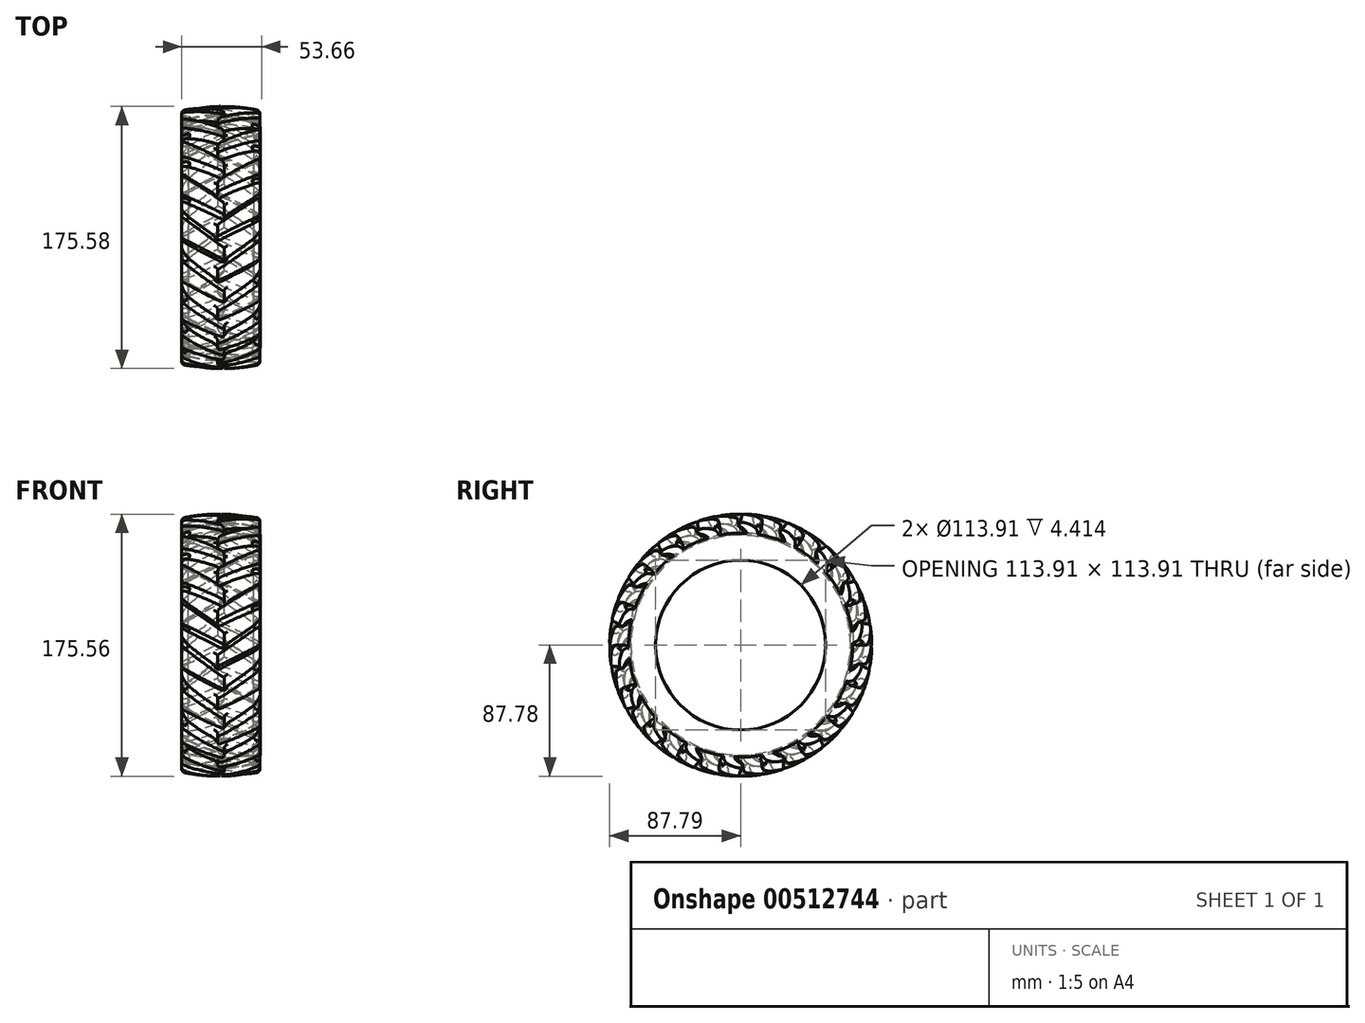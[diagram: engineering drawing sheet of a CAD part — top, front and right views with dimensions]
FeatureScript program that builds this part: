
annotation { "Feature Type Name" : "Feature", "Feature Type Description" : "" }
export const myFeature = defineFeature(function(context is Context, id is Id, definition is map)
    precondition{}
    {
        {
            var Q0;
            Q0=qCreatedBy(makeId("Top.planeOp"),FACE);
            var sketch = newSketch(context, id + "F0", { "sketchPlane" : qUnion([Q0])});
            skLineSegment(sketch, "E0", {"start": v(-41.36, 0) * mm, "end": v(39.08, 0) * mm});
            skLineSegment(sketch, "E1", {"start": v(0, 0) * mm, "end": v(0, 69.17) * mm});
            skLineSegment(sketch, "E2.bottom", {"start": v(26.28, 56.34) * mm, "end": v(-26.28, 56.34) * mm});
            skLineSegment(sketch, "E2.left", {"start": v(26.28, 56.34) * mm, "end": v(26.28, 73.43) * mm});
            skLineSegment(sketch, "E2.right", {"start": v(-26.28, 56.34) * mm, "end": v(-26.28, 73.43) * mm});
            skPoint(sketch, "E2.middle", {"position": v(0, 69.17) * mm});
            skArc(sketch, "E3", {"start": v(-21.6, 79.56) * mm, "mid": v(0, 82.44) * mm, "end": v(21.6, 79.56) * mm});
            skPoint(sketch, "E4.orphan", {"position": v(-26.28, 82) * mm});
            skPoint(sketch, "E5.orphan", {"position": v(26.28, 82) * mm});
            skPoint(sketch, "E6.visualSharp", {"position": v(-26.28, 78.14) * mm});
            skArc(sketch, "E6.filletArc", {"start": v(-21.6, 79.56) * mm, "mid": v(-24.97, 77.3) * mm, "end": v(-26.28, 73.43) * mm});
            skPoint(sketch, "E7.visualSharp", {"position": v(26.28, 78.14) * mm});
            skArc(sketch, "E7.filletArc", {"start": v(26.28, 73.43) * mm, "mid": v(24.97, 77.3) * mm, "end": v(21.6, 79.56) * mm});
            skSolve(sketch);
        }
        {
            var Q0;
            Q0=qSketchRegion(id+"F0",true);
            var Q1;
            Q1=sQuery(id+"F0.wireOp",EDGE,"E0");
            revolve(context, id + "F1", {"entities" : qUnion([Q0]), "axis" : qUnion([Q1]), "revolveType" : RevolveType.FULL});
        }
        {
            var Q0;
            Q0=qCreatedBy(makeId("Top.planeOp"),FACE);
            var sketch = newSketch(context, id + "F2", { "sketchPlane" : qUnion([Q0])});
            skLineSegment(sketch, "E8", {"start": v(-26.25, 13.83) * mm, "end": v(2.16, -6.94) * mm});
            skLineSegment(sketch, "E9", {"start": v(2.16, -6.94) * mm, "end": v(2.16, -14.96) * mm});
            skLineSegment(sketch, "E10", {"start": v(2.16, -14.96) * mm, "end": v(-26.25, -0.3) * mm});
            skLineSegment(sketch, "E11", {"start": v(-26.25, 13.83) * mm, "end": v(-26.25, 0) * mm});
            skLineSegment(sketch, "E12", {"start": v(-26.25, 0) * mm, "end": v(-26.25, -0.3) * mm});
            skPoint(sketch, "E13.orphan", {"position": v(-26.83, 0) * mm});
            skLineSegment(sketch, "E14", {"start": v(-49.96, 0) * mm, "end": v(51.5, 0) * mm});
            skSolve(sketch);
        }
        {
            var Q0;
            Q0=makeQuery(id+"F2.imprint","IMPRINT",FACE,{"disambiguationData":[TD([[makeQuery(id+"F2.imprint","IMPRINT",EDGE,{"derivedFrom":sQuery(id+"F2.wireOp",EDGE,"E8")}),-1.0]])]});
            var Q1;
            {var subQ1=sQuery(id+"F2.wireOp",EDGE,"E9");Q1=makeQuery(id+"F2.imprint","IMPRINT",FACE,{"disambiguationData":[TD([[makeQuery(id+"F2.imprint","IMPRINT",EDGE,{"derivedFrom":subQ1}),-1.0]])]});}
            extrude(context, id + "F3", {"entities" : qUnion([Q0, Q1]), "operationType" : NewBodyOperationType.ADD, "depth" : 88.9 * mm});
        }
        {
            var Q0;
            Q0=qCreatedBy(makeId("Top.planeOp"),FACE);
            var Q1;
            Q1=sQuery(id+"F2.wireOp",EDGE,"E14");
            cPlane(context, id + "F4", {"entities" : qUnion([Q0, Q1]), "cplaneType" : CPlaneType.LINE_ANGLE, "offset" : 152.4 * mm, "angle" : 10 * degree, "width" : 152.4 * mm, "height" : 152.4 * mm});
        }
        {
            var Q0;
            Q0=qCreatedBy(id+"F4.planeOp",FACE);
            var sketch = newSketch(context, id + "F5", { "sketchPlane" : qUnion([Q0])});
            skLineSegment(sketch, "E15", {"start": v(-2.2, 14.33) * mm, "end": v(-2.2, 6.63) * mm});
            skLineSegment(sketch, "E16", {"start": v(-2.2, 6.63) * mm, "end": v(26.07, -12.68) * mm});
            skLineSegment(sketch, "E17", {"start": v(26.07, -12.68) * mm, "end": v(26.07, 0) * mm});
            skLineSegment(sketch, "E18", {"start": v(26.07, 0) * mm, "end": v(-2.2, 14.33) * mm});
            skSolve(sketch);
        }
        {
            var Q0;
            Q0=makeQuery(id+"F5.imprint","IMPRINT",FACE,{"disambiguationData":[TD([[makeQuery(id+"F5.imprint","IMPRINT",EDGE,{"derivedFrom":sQuery(id+"F5.wireOp",EDGE,"E15")}),1.0]])]});
            extrude(context, id + "F6", {"entities" : qUnion([Q0]), "operationType" : NewBodyOperationType.ADD, "oppositeDirection" : true, "depth" : 88.9 * mm});
        }
        {
            var Q0;
            Q0=qCreatedBy(makeId("Front.planeOp"),FACE);
            var sketch = newSketch(context, id + "F7", { "sketchPlane" : qUnion([Q0])});
            skArc(sketch, "E19", {"start": v(33.67, -83.2) * mm, "mid": v(-0.3, -87.8) * mm, "end": v(-34.27, -83.04) * mm});
            skLineSegment(sketch, "E20", {"start": v(-34.27, -83.04) * mm, "end": v(-34.27, -99.42) * mm});
            skLineSegment(sketch, "E21", {"start": v(-34.27, -99.42) * mm, "end": v(37.55, -99.42) * mm});
            skLineSegment(sketch, "E22", {"start": v(37.55, -99.42) * mm, "end": v(33.67, -83.2) * mm});
            skArc(sketch, "E23", {"start": v(21.86, -73.58) * mm, "mid": v(0, -75.71) * mm, "end": v(-21.86, -73.58) * mm});
            skLineSegment(sketch, "E24", {"start": v(-21.86, -73.58) * mm, "end": v(-21.86, -56.95) * mm});
            skLineSegment(sketch, "E25", {"start": v(-21.86, 0) * mm, "end": v(21.86, 0) * mm});
            skLineSegment(sketch, "E26", {"start": v(21.86, -56.95) * mm, "end": v(21.86, -73.58) * mm});
            skLineSegment(sketch, "E27", {"start": v(21.86, -56.95) * mm, "end": v(33.74, -56.95) * mm});
            skLineSegment(sketch, "E28", {"start": v(33.74, -56.95) * mm, "end": v(33.74, 0) * mm});
            skLineSegment(sketch, "E29", {"start": v(33.74, 0) * mm, "end": v(21.86, 0) * mm});
            skLineSegment(sketch, "E30", {"start": v(0, 0) * mm, "end": v(0, -57.21) * mm});
            skPoint(sketch, "E30.endSnap0", {"position": v(0, 0) * mm});
            skLineSegment(sketch, "E31.MirrorCS", {"start": v(-21.86, -56.95) * mm, "end": v(-33.74, -56.95) * mm});
            skLineSegment(sketch, "E32.MirrorCS", {"start": v(-33.74, -56.95) * mm, "end": v(-33.74, 0) * mm});
            skLineSegment(sketch, "E33.MirrorCS", {"start": v(-33.74, 0) * mm, "end": v(-21.86, 0) * mm});
            skSolve(sketch);
        }
        {
            var Q0;
            Q0=qSketchRegion(id+"F7",true);
            var Q1;
            Q1=sQuery(id+"F2.wireOp",EDGE,"E14");
            revolve(context, id + "F8", {"operationType" : NewBodyOperationType.REMOVE, "entities" : qUnion([Q0]), "axis" : qUnion([Q1]), "revolveType" : RevolveType.FULL, "oppositeDirection" : true});
        }
        {
            var Q0;
            Q0=makeQuery(id+"F6.boolean.opBoolean","INTERSECT",EDGE,{"derivedFrom":[makeQuery(id+"F1.opRevolve","SWEPT_FACE",FACE,{"disambiguationData":[OSD([sQuery(id+"F0.wireOp",EDGE,"E3")])]}),makeQuery(id+"F6.opExtrude","SWEPT_FACE",FACE,{"disambiguationData":[OSD([sQuery(id+"F5.wireOp",EDGE,"E18")])]})]});
            var Q1;
            Q1=makeQuery(id+"F6.boolean.opBoolean","INTERSECT",EDGE,{"derivedFrom":[makeQuery(id+"F1.opRevolve","SWEPT_FACE",FACE,{"disambiguationData":[OSD([sQuery(id+"F0.wireOp",EDGE,"E3")])]}),makeQuery(id+"F6.opExtrude","SWEPT_FACE",FACE,{"disambiguationData":[OSD([sQuery(id+"F5.wireOp",EDGE,"E16")])]})]});
            var Q2;
            Q2=makeQuery(id+"F3.boolean.opBoolean","INTERSECT",EDGE,{"derivedFrom":[makeQuery(id+"F1.opRevolve","SWEPT_FACE",FACE,{"disambiguationData":[OSD([sQuery(id+"F0.wireOp",EDGE,"E3")])]}),makeQuery(id+"F3.opExtrude","SWEPT_FACE",FACE,{"disambiguationData":[OSD([sQuery(id+"F2.wireOp",EDGE,"E8")])]})]});
            var Q3;
            Q3=makeQuery(id+"F3.boolean.opBoolean","INTERSECT",EDGE,{"derivedFrom":[makeQuery(id+"F1.opRevolve","SWEPT_FACE",FACE,{"disambiguationData":[OSD([sQuery(id+"F0.wireOp",EDGE,"E3")])]}),makeQuery(id+"F3.opExtrude","SWEPT_FACE",FACE,{"disambiguationData":[OSD([sQuery(id+"F2.wireOp",EDGE,"E10")])]})]});
            var Q4;
            Q4=makeQuery(id+"F6.boolean.opBoolean","INTERSECT",EDGE,{"derivedFrom":[makeQuery(id+"F1.opRevolve","SWEPT_FACE",FACE,{"disambiguationData":[OSD([sQuery(id+"F0.wireOp",EDGE,"E3")])]}),makeQuery(id+"F6.opExtrude","SWEPT_FACE",FACE,{"disambiguationData":[OSD([sQuery(id+"F5.wireOp",EDGE,"E15")])]})]});
            var Q5;
            Q5=makeQuery(id+"F3.boolean.opBoolean","INTERSECT",EDGE,{"derivedFrom":[makeQuery(id+"F1.opRevolve","SWEPT_FACE",FACE,{"disambiguationData":[OSD([sQuery(id+"F0.wireOp",EDGE,"E3")])]}),makeQuery(id+"F3.opExtrude","SWEPT_FACE",FACE,{"disambiguationData":[OSD([sQuery(id+"F2.wireOp",EDGE,"E9")])]})]});
            var Q6;
            {var subQ2=sQuery(id+"F2.wireOp",EDGE,"E12");var subQ3=sQuery(id+"F2.wireOp",EDGE,"E11");Q6=makeQuery(id+"F8.boolean.opBoolean","INTERSECT",EDGE,{"derivedFrom":[makeQuery(id+"F3.boolean.opBoolean","SPLIT",FACE,{"disambiguationData":[TD([makeQuery(id+"F1.opRevolve","SWEPT_FACE",FACE,{"disambiguationData":[OSD([sQuery(id+"F0.wireOp",EDGE,"E6.filletArc")])]})])],"derivedFrom":makeQuery(id+"F3.opExtrude","SWEPT_FACE",FACE,{"disambiguationData":[OSD([subQ3,subQ2])]})}),makeQuery(id+"F8.opRevolve","SWEPT_FACE",FACE,{"disambiguationData":[OSD([sQuery(id+"F7.wireOp",EDGE,"E19")])]})]});}
            var Q7;
            {var subQ2=sQuery(id+"F2.wireOp",EDGE,"E9");Q7=makeQuery(id+"F8.boolean.opBoolean","INTERSECT",EDGE,{"derivedFrom":[makeQuery(id+"F3.boolean.opBoolean","SPLIT",FACE,{"disambiguationData":[TD([makeQuery(id+"F1.opRevolve","SWEPT_FACE",FACE,{"disambiguationData":[OSD([sQuery(id+"F0.wireOp",EDGE,"E3")])]})])],"derivedFrom":makeQuery(id+"F3.opExtrude","SWEPT_FACE",FACE,{"disambiguationData":[OSD([subQ2])]})}),makeQuery(id+"F8.opRevolve","SWEPT_FACE",FACE,{"disambiguationData":[OSD([sQuery(id+"F7.wireOp",EDGE,"E19")])]})]});}
            var Q8;
            {var subQ2=sQuery(id+"F5.wireOp",EDGE,"E15");Q8=makeQuery(id+"F8.boolean.opBoolean","INTERSECT",EDGE,{"derivedFrom":[makeQuery(id+"F6.boolean.opBoolean","SPLIT",FACE,{"disambiguationData":[TD([makeQuery(id+"F1.opRevolve","SWEPT_FACE",FACE,{"disambiguationData":[OSD([sQuery(id+"F0.wireOp",EDGE,"E3")])]})])],"derivedFrom":makeQuery(id+"F6.opExtrude","SWEPT_FACE",FACE,{"disambiguationData":[OSD([subQ2])]})}),makeQuery(id+"F8.opRevolve","SWEPT_FACE",FACE,{"disambiguationData":[OSD([sQuery(id+"F7.wireOp",EDGE,"E19")])]})]});}
            var Q9;
            {var subQ2=sQuery(id+"F5.wireOp",EDGE,"E17");Q9=makeQuery(id+"F8.boolean.opBoolean","INTERSECT",EDGE,{"derivedFrom":[makeQuery(id+"F6.boolean.opBoolean","SPLIT",FACE,{"disambiguationData":[TD([makeQuery(id+"F1.opRevolve","SWEPT_FACE",FACE,{"disambiguationData":[OSD([sQuery(id+"F0.wireOp",EDGE,"E7.filletArc")])]})])],"derivedFrom":makeQuery(id+"F6.opExtrude","SWEPT_FACE",FACE,{"disambiguationData":[OSD([subQ2])]})}),makeQuery(id+"F8.opRevolve","SWEPT_FACE",FACE,{"disambiguationData":[OSD([sQuery(id+"F7.wireOp",EDGE,"E19")])]})]});}
            fillet(context, id + "F9", {"entities" : qUnion([Q0, Q1, Q2, Q3, Q4, Q5, Q6, Q7, Q8, Q9]), "radius" : 2.54 * mm, "tangentPropagation" : true, "allowEdgeOverflow" : false});
        }
        {
            var Q0;
            Q0=makeQuery(id+"F1.opRevolve","SWEPT_BODY",BODY,{"disambiguationData":[OSD([sQuery(id+"F0.wireOp",EDGE,"E2.bottom"),sQuery(id+"F0.wireOp",EDGE,"E2.left"),sQuery(id+"F0.wireOp",EDGE,"E2.right"),sQuery(id+"F0.wireOp",EDGE,"E3"),sQuery(id+"F0.wireOp",EDGE,"E6.filletArc"),sQuery(id+"F0.wireOp",EDGE,"E7.filletArc")])]});
            var Q1;
            Q1=sQuery(id+"F2.wireOp",EDGE,"E14");
            circularPattern(context, id + "F10", {"operationType" : NewBodyOperationType.ADD, "entities" : qUnion([Q0]), "axis" : qUnion([Q1]), "angle" : 20 * degree, "instanceCount" : 18});
        }
    });
